# Revit family: Hager-Univers-IP44-D205-H950-Cl.II-Encl-NoHosted-DE-de
name_source: partatom
category: Equipement électrique
units: mm (PartAtom-declared; Revit-internal decimal feet)

## family parameters
Basée sur le plan de construction = Oui
Configuration du panneau = Deux colonnes, circuits au sein
Cote de connecteur circulaire = Utiliser le diamètre
Couper avec des vides une fois chargée = Non
Partagée = Non
Point de calcul de pièce = Non
Toujours verticalement = Oui
Type d'élément = Tableau de raccordement

## types (5) — shared parameters
Commentaires du type = Univers
EF000003 - Montageart = EV000384 - Aufputz
EF000007 - Farbe = EV000202 - weiß
EF000040 - Höhe = 950 mm  [stored 3.1168 ft]
EF000049 - Tiefe = 205 mm  [stored 0.672572 ft]
EF000116 - RAL-Nummer = 9010
EF000118 - Mit Montageplatte = Non
EF000218 - Einbautiefe = 205 mm  [stored 0.672572 ft]
EF000266 - Anzahl der Reihen = 6
EF001088 - Anbaumöglichkeit = Oui
EF001596 - Werkstoff des Gehäuses = EV000179 - Stahl
EF001613 - Funktionserhalt = EV000494 - ohne
EF003532 - Geeignet für Außengebrauch = Non
EF004293 - Schlagfestigkeit = EV006815 - IK09
EF005474 - Schutzart (IP) = EV006418 - IP44
EF006244 - Transparenter Deckel/Tür = Non
EF006306 - Mit Schloss = Non
EF007800 - Geeignet für Blitzschutz = Non
EF008873 - Nennstrom (In) = 250 A
EF009170 - Materialstärke Gehäuse = 1 mm  [stored 0.00328084 ft]
EF009171 - Materialstärke Tür/Deckel = 1 mm  [stored 0.00328084 ft]
EF009212 - Ausführung Deckel = EV000116 - geschlossen
EF015940 - Deckel mit Überdruckentlastung = Non
Elévation par défaut = 1219 mm
Fabricant = Hager
HG000002 - Mit tür = Oui
HG000003 - Bereich = Univers
HG000006 - Unterputz = Non
HG000023 - Gehäuse mit doppeltem Querschnitt = Non
HG000024 - Höhe des unteren Teils = 600 mm
HG000026 - Stehend auf dem Boden = Non
zero-valued in all types: HG000027 - Sockelhöhe

## per-type parameters (varying)
| type | EF000008 - Breite | EF000339 - Art der Abdeckung | EF000437 - Anzahl der Leitungseinführungen | EF001131 - Innentiefe | EF002950 - Breite in Teilungseinheiten | EF004427 - Anzahl der Module | EF004464 - Art der Tür | EF009554 - Anzahl der Öffnungen für Flanschplatten | HG000004 - Herstellerreferenz | HG000009 - Doppelflügeligen Tür | HG000010 - Asymmetrische Türen |
| Aufputz IP44 B1050 H950 T205  - FP64SN2 | 1050 mm | EV004216 - Tür | 8 | 130 mm  [stored 0.426509 ft] | 48 | 288 | EV003602 - Doppel | 8 | FP64SN2 | Oui | Non |
| Aufputz IP44 B1300 H950 T205  - FP65SN2 | 1300 mm  [stored 4.26509 ft] | EV004216 - Tür | 10 | 130 mm  [stored 0.426509 ft] | 60 | 360 | EV003602 - Doppel | 10 | FP65SN2 | Oui | Oui |
| Aufputz IP44 B300 H950 T205  - FP61SN2 | 300 mm | EV001012 - Deckel | 2 | 143 mm | 12 | 72 | EV002646 - Einzel | 2 | FP61SN2 | Non | Non |
| Aufputz IP44 B550 H950 T205  - FP62SN2 | 550 mm | EV001012 - Deckel | 4 | 143 mm | 24 | 144 | EV002646 - Einzel | 4 | FP62SN2 | Non | Non |
| Aufputz IP44 B800 H950 T205  - FP63SN2 | 800 mm  [stored 2.62467 ft] | EV004216 - Tür | 6 | 130 mm  [stored 0.426509 ft] | 36 | 216 | EV002646 - Einzel | 6 | FP63SN2 | Non | Non |

note: [stored X ft] marks values corroborated as IEEE doubles in the binary element streams (Revit-internal decimal feet)

## geometry (parser evidence)
native form markers: Blend x4, Sweep x11
no freeform markers — native parametric forms only
